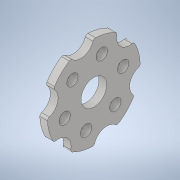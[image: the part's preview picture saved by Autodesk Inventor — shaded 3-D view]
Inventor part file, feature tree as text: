
AUTODESK INVENTOR PART (.ipt)
format: ipt  version: 2021 (Build 250183000, 183)  size: 174,080 bytes
history: native  units: in
note: dims shown in document units (in); Inventor stores cm internally (conversion verified against a paired STEP export)
features: extrude x1, fillet x1, sketch x1
ambient origin geometry x8: Origin, YZ Plane, XZ Plane, XY Plane, X Axis, Y Axis, Z Axis, Center Point
bodies: Solid1 (feature_tree)
feature tree (3):
  extrude  "Extrusion1"  Depth=0.125in
  fillet  "Fillet1"  Radius=0.55in
  sketch  "Sketch1"  dims[d0=4.517in d1=2.952in d2=0.55in d3=45.0deg d4=2.3622in d6=360.0deg d8=1.25in d12=1.25in d16=15.0deg d17=2.3622in d19=360.0deg d21=0.375in d22=0.0in d23=0.125in]
